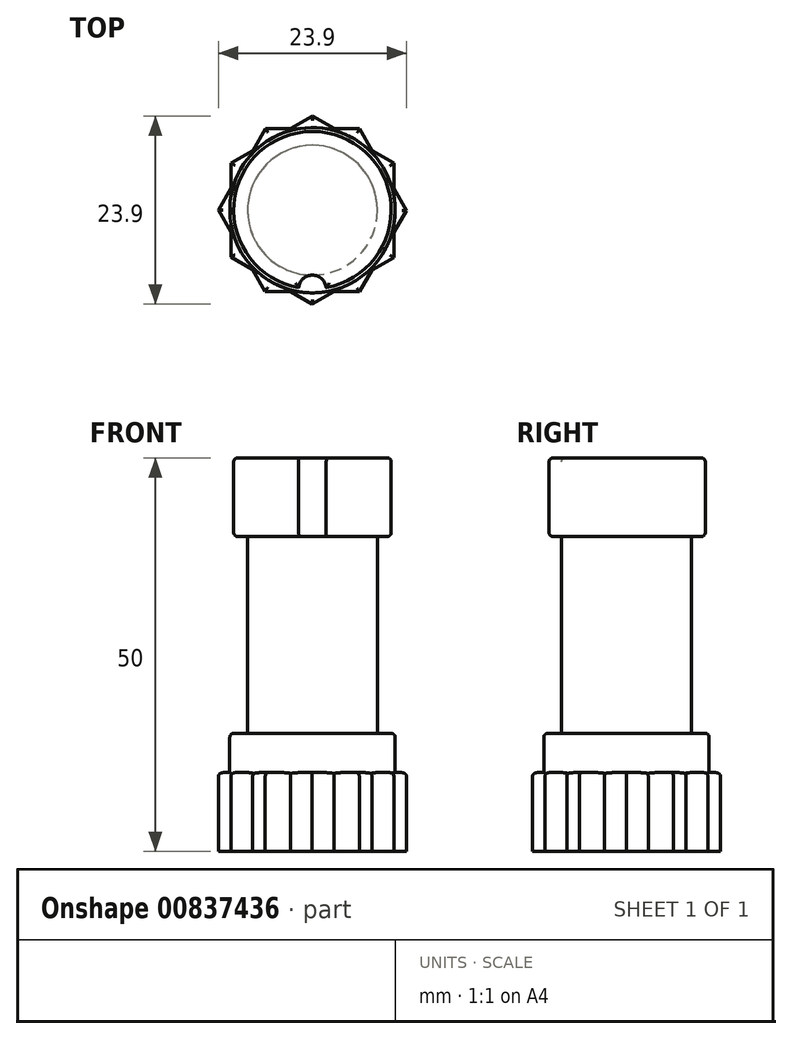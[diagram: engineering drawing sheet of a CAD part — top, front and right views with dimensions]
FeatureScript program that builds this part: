
annotation { "Feature Type Name" : "Feature", "Feature Type Description" : "" }
export const myFeature = defineFeature(function(context is Context, id is Id, definition is map)
    precondition{}
    {
        {
            var Q0;
            Q0=qCreatedBy(makeId("Top.planeOp"),FACE);
            var sketch = newSketch(context, id + "F0", { "sketchPlane" : qUnion([Q0])});
            skCircle(sketch, "E0.cCircle", {"center": v(0, 0) * mm, "radius": 11.95 * mm, "construction": true});
            skLineSegment(sketch, "E0.0", {"start": v(10.36, 5.96) * mm, "end": v(10.36, 2.75) * mm});
            skLineSegment(sketch, "E0.1", {"start": v(10.34, -6) * mm, "end": v(7.56, -7.6) * mm});
            skLineSegment(sketch, "E0.2", {"start": v(-0.02, -11.95) * mm, "end": v(-2.8, -10.34) * mm});
            skLineSegment(sketch, "E0.3", {"start": v(-10.36, -5.96) * mm, "end": v(-10.36, -2.75) * mm});
            skLineSegment(sketch, "E0.4", {"start": v(-10.34, 6) * mm, "end": v(-7.56, 7.6) * mm});
            skLineSegment(sketch, "E0.5", {"start": v(0.02, 11.95) * mm, "end": v(2.8, 10.34) * mm});
            skLineSegment(sketch, "E1", {"start": v(6, 10.34) * mm, "end": v(6.72, 11.59) * mm, "construction": true});
            skLineSegment(sketch, "E2.0", {"start": v(6, 10.34) * mm, "end": v(7.6, 7.56) * mm});
            skLineSegment(sketch, "E2.1", {"start": v(11.95, -0.02) * mm, "end": v(10.34, -2.8) * mm});
            skLineSegment(sketch, "E2.2", {"start": v(5.96, -10.36) * mm, "end": v(2.75, -10.36) * mm});
            skLineSegment(sketch, "E2.3", {"start": v(-6, -10.34) * mm, "end": v(-7.6, -7.56) * mm});
            skLineSegment(sketch, "E2.4", {"start": v(-11.95, 0.02) * mm, "end": v(-10.34, 2.8) * mm});
            skLineSegment(sketch, "E2.5", {"start": v(-5.96, 10.36) * mm, "end": v(-2.75, 10.36) * mm});
            skLineSegment(sketch, "E3.trimOffspring", {"start": v(-7.6, -7.56) * mm, "end": v(-10.36, -5.96) * mm});
            skPoint(sketch, "E4.orphan", {"position": v(-5.2, -8.95) * mm});
            skLineSegment(sketch, "E5.trimOffspring", {"start": v(-10.36, -2.75) * mm, "end": v(-11.95, 0.02) * mm});
            skLineSegment(sketch, "E6.trimOffspring", {"start": v(-2.8, -10.34) * mm, "end": v(-6, -10.34) * mm});
            skLineSegment(sketch, "E7.trimOffspring", {"start": v(2.75, -10.36) * mm, "end": v(-0.02, -11.95) * mm});
            skLineSegment(sketch, "E8.trimOffspring", {"start": v(7.56, -7.6) * mm, "end": v(5.96, -10.36) * mm});
            skLineSegment(sketch, "E9.trimOffspring", {"start": v(-10.34, 2.8) * mm, "end": v(-10.34, 6) * mm});
            skLineSegment(sketch, "E10.trimOffspring", {"start": v(-7.56, 7.6) * mm, "end": v(-5.96, 10.36) * mm});
            skLineSegment(sketch, "E11.trimOffspring", {"start": v(-2.75, 10.36) * mm, "end": v(0.02, 11.95) * mm});
            skLineSegment(sketch, "E12.trimOffspring", {"start": v(2.8, 10.34) * mm, "end": v(6, 10.34) * mm});
            skLineSegment(sketch, "E13.trimOffspring", {"start": v(7.6, 7.56) * mm, "end": v(10.36, 5.96) * mm});
            skPoint(sketch, "E14.orphan", {"position": v(5.2, 8.95) * mm});
            skLineSegment(sketch, "E15.trimOffspring", {"start": v(10.36, 2.75) * mm, "end": v(11.95, -0.02) * mm});
            skLineSegment(sketch, "E16.trimOffspring", {"start": v(10.34, -2.8) * mm, "end": v(10.34, -6) * mm});
            skSolve(sketch);
        }
        {
            var Q0;
            Q0=makeQuery(id+"F0.imprint","IMPRINT",FACE,{"disambiguationData":[TD([[makeQuery(id+"F0.imprint","IMPRINT",EDGE,{"derivedFrom":sQuery(id+"F0.wireOp",EDGE,"E0.0")}),-1.0]])]});
            extrude(context, id + "F1", {"entities" : qUnion([Q0]), "depth" : 10 * mm, "offsetDistance" : 25 * mm});
        }
        {
            var Q0;
            Q0=makeQuery(id+"F1.opExtrude","CAP_FACE",FACE,{"disambiguationData":[OSD([sQuery(id+"F0.wireOp",EDGE,"E0.0"),sQuery(id+"F0.wireOp",EDGE,"E0.1"),sQuery(id+"F0.wireOp",EDGE,"E0.2"),sQuery(id+"F0.wireOp",EDGE,"E0.3"),sQuery(id+"F0.wireOp",EDGE,"E0.4"),sQuery(id+"F0.wireOp",EDGE,"E0.5"),sQuery(id+"F0.wireOp",EDGE,"E2.0"),sQuery(id+"F0.wireOp",EDGE,"E2.1"),sQuery(id+"F0.wireOp",EDGE,"E2.2"),sQuery(id+"F0.wireOp",EDGE,"E2.3"),sQuery(id+"F0.wireOp",EDGE,"E2.4"),sQuery(id+"F0.wireOp",EDGE,"E2.5"),sQuery(id+"F0.wireOp",EDGE,"E3.trimOffspring"),sQuery(id+"F0.wireOp",EDGE,"E5.trimOffspring"),sQuery(id+"F0.wireOp",EDGE,"E6.trimOffspring"),sQuery(id+"F0.wireOp",EDGE,"E7.trimOffspring"),sQuery(id+"F0.wireOp",EDGE,"E8.trimOffspring"),sQuery(id+"F0.wireOp",EDGE,"E9.trimOffspring"),sQuery(id+"F0.wireOp",EDGE,"E10.trimOffspring"),sQuery(id+"F0.wireOp",EDGE,"E11.trimOffspring"),sQuery(id+"F0.wireOp",EDGE,"E12.trimOffspring"),sQuery(id+"F0.wireOp",EDGE,"E13.trimOffspring"),sQuery(id+"F0.wireOp",EDGE,"E15.trimOffspring"),sQuery(id+"F0.wireOp",EDGE,"E16.trimOffspring")])],"isStart":false});
            var sketch = newSketch(context, id + "F2", { "sketchPlane" : qUnion([Q0])});
            skLineSegment(sketch, "E17", {"start": v(-10.36, -2.75) * mm, "end": v(10.36, 2.75) * mm, "construction": true});
            skLineSegment(sketch, "E18", {"start": v(2.75, -10.36) * mm, "end": v(-2.75, 10.36) * mm, "construction": true});
            skCircle(sketch, "E19", {"center": v(0, 0) * mm, "radius": 10.5 * mm});
            skSolve(sketch);
        }
        {
            var Q0;
            Q0=makeQuery(id+"F2.imprint","IMPRINT",FACE,{"disambiguationData":[TD([[makeQuery(id+"F2.imprint","IMPRINT",EDGE,{"derivedFrom":sQuery(id+"F2.wireOp",EDGE,"E19")}),1.0]])]});
            extrude(context, id + "F3", {"entities" : qUnion([Q0]), "operationType" : NewBodyOperationType.ADD, "depth" : 5 * mm, "offsetDistance" : 25 * mm});
        }
        {
            var Q0;
            Q0=makeQuery(id+"F1.opExtrude","CAP_EDGE",EDGE,{"disambiguationData":[OSD([sQuery(id+"F0.wireOp",EDGE,"E2.5")])],"isStart":false});
            var Q1;
            Q1=makeQuery(id+"F1.opExtrude","CAP_EDGE",EDGE,{"disambiguationData":[OSD([sQuery(id+"F0.wireOp",EDGE,"E10.trimOffspring")])],"isStart":false});
            var Q2;
            Q2=makeQuery(id+"F1.opExtrude","CAP_EDGE",EDGE,{"disambiguationData":[OSD([sQuery(id+"F0.wireOp",EDGE,"E0.4")])],"isStart":false});
            var Q3;
            Q3=makeQuery(id+"F1.opExtrude","CAP_EDGE",EDGE,{"disambiguationData":[OSD([sQuery(id+"F0.wireOp",EDGE,"E9.trimOffspring")])],"isStart":false});
            var Q4;
            Q4=makeQuery(id+"F1.opExtrude","CAP_EDGE",EDGE,{"disambiguationData":[OSD([sQuery(id+"F0.wireOp",EDGE,"E2.4")])],"isStart":false});
            var Q5;
            Q5=makeQuery(id+"F1.opExtrude","CAP_EDGE",EDGE,{"disambiguationData":[OSD([sQuery(id+"F0.wireOp",EDGE,"E5.trimOffspring")])],"isStart":false});
            var Q6;
            Q6=makeQuery(id+"F1.opExtrude","CAP_EDGE",EDGE,{"disambiguationData":[OSD([sQuery(id+"F0.wireOp",EDGE,"E0.3")])],"isStart":false});
            var Q7;
            Q7=makeQuery(id+"F1.opExtrude","CAP_EDGE",EDGE,{"disambiguationData":[OSD([sQuery(id+"F0.wireOp",EDGE,"E3.trimOffspring")])],"isStart":false});
            var Q8;
            Q8=makeQuery(id+"F1.opExtrude","CAP_EDGE",EDGE,{"disambiguationData":[OSD([sQuery(id+"F0.wireOp",EDGE,"E2.3")])],"isStart":false});
            var Q9;
            Q9=makeQuery(id+"F1.opExtrude","CAP_EDGE",EDGE,{"disambiguationData":[OSD([sQuery(id+"F0.wireOp",EDGE,"E6.trimOffspring")])],"isStart":false});
            var Q10;
            Q10=makeQuery(id+"F1.opExtrude","CAP_EDGE",EDGE,{"disambiguationData":[OSD([sQuery(id+"F0.wireOp",EDGE,"E0.2")])],"isStart":false});
            var Q11;
            Q11=makeQuery(id+"F1.opExtrude","CAP_EDGE",EDGE,{"disambiguationData":[OSD([sQuery(id+"F0.wireOp",EDGE,"E7.trimOffspring")])],"isStart":false});
            var Q12;
            Q12=makeQuery(id+"F1.opExtrude","CAP_EDGE",EDGE,{"disambiguationData":[OSD([sQuery(id+"F0.wireOp",EDGE,"E2.2")])],"isStart":false});
            var Q13;
            Q13=makeQuery(id+"F1.opExtrude","CAP_EDGE",EDGE,{"disambiguationData":[OSD([sQuery(id+"F0.wireOp",EDGE,"E8.trimOffspring")])],"isStart":false});
            var Q14;
            Q14=makeQuery(id+"F1.opExtrude","CAP_EDGE",EDGE,{"disambiguationData":[OSD([sQuery(id+"F0.wireOp",EDGE,"E0.1")])],"isStart":false});
            var Q15;
            Q15=makeQuery(id+"F1.opExtrude","CAP_EDGE",EDGE,{"disambiguationData":[OSD([sQuery(id+"F0.wireOp",EDGE,"E16.trimOffspring")])],"isStart":false});
            var Q16;
            Q16=makeQuery(id+"F1.opExtrude","CAP_EDGE",EDGE,{"disambiguationData":[OSD([sQuery(id+"F0.wireOp",EDGE,"E2.1")])],"isStart":false});
            var Q17;
            Q17=makeQuery(id+"F1.opExtrude","CAP_EDGE",EDGE,{"disambiguationData":[OSD([sQuery(id+"F0.wireOp",EDGE,"E15.trimOffspring")])],"isStart":false});
            var Q18;
            Q18=makeQuery(id+"F1.opExtrude","CAP_EDGE",EDGE,{"disambiguationData":[OSD([sQuery(id+"F0.wireOp",EDGE,"E0.0")])],"isStart":false});
            var Q19;
            Q19=makeQuery(id+"F1.opExtrude","CAP_EDGE",EDGE,{"disambiguationData":[OSD([sQuery(id+"F0.wireOp",EDGE,"E13.trimOffspring")])],"isStart":false});
            var Q20;
            Q20=makeQuery(id+"F1.opExtrude","CAP_EDGE",EDGE,{"disambiguationData":[OSD([sQuery(id+"F0.wireOp",EDGE,"E2.0")])],"isStart":false});
            var Q21;
            Q21=makeQuery(id+"F1.opExtrude","CAP_EDGE",EDGE,{"disambiguationData":[OSD([sQuery(id+"F0.wireOp",EDGE,"E12.trimOffspring")])],"isStart":false});
            var Q22;
            Q22=makeQuery(id+"F1.opExtrude","CAP_EDGE",EDGE,{"disambiguationData":[OSD([sQuery(id+"F0.wireOp",EDGE,"E0.5")])],"isStart":false});
            var Q23;
            Q23=makeQuery(id+"F1.opExtrude","CAP_EDGE",EDGE,{"disambiguationData":[OSD([sQuery(id+"F0.wireOp",EDGE,"E11.trimOffspring")])],"isStart":false});
            fillet(context, id + "F4", {"entities" : qUnion([Q0, Q1, Q2, Q3, Q4, Q5, Q6, Q7, Q8, Q9, Q10, Q11, Q12, Q13, Q14, Q15, Q16, Q17, Q18, Q19, Q20, Q21, Q22, Q23]), "radius" : .5 * mm, "tangentPropagation" : true, "allowEdgeOverflow" : false});
        }
        {
            var Q0;
            Q0=makeQuery(id+"F3.opExtrude","CAP_FACE",FACE,{"disambiguationData":[OSD([sQuery(id+"F2.wireOp",EDGE,"E19")])],"isStart":false});
            var sketch = newSketch(context, id + "F5", { "sketchPlane" : qUnion([Q0])});
            skCircle(sketch, "E20", {"center": v(0, 0) * mm, "radius": 8.25 * mm});
            skSolve(sketch);
        }
        {
            var Q0;
            Q0=makeQuery(id+"F5.imprint","IMPRINT",FACE,{"disambiguationData":[TD([[makeQuery(id+"F5.imprint","IMPRINT",EDGE,{"derivedFrom":sQuery(id+"F5.wireOp",EDGE,"E20")}),1.0]])]});
            extrude(context, id + "F6", {"entities" : qUnion([Q0]), "operationType" : NewBodyOperationType.ADD, "depth" : 25 * mm, "offsetDistance" : 25 * mm});
        }
        {
            var Q0;
            Q0=makeQuery(id+"F6.opExtrude","CAP_FACE",FACE,{"disambiguationData":[OSD([sQuery(id+"F5.wireOp",EDGE,"E20")])],"isStart":false});
            var sketch = newSketch(context, id + "F7", { "sketchPlane" : qUnion([Q0])});
            skCircle(sketch, "E21", {"center": v(0, 0) * mm, "radius": 10 * mm});
            skSolve(sketch);
        }
        {
            var Q0;
            Q0=makeQuery(id+"F7.imprint","IMPRINT",FACE,{"disambiguationData":[TD([[makeQuery(id+"F7.imprint","IMPRINT",EDGE,{"derivedFrom":sQuery(id+"F7.wireOp",EDGE,"E21")}),1.0]])]});
            var Q1;
            Q1=makeQuery(id+"F7.imprint","IMPRINT",FACE,{"disambiguationData":[TD([[makeQuery(id+"F7.imprint","IMPRINT",EDGE,{"derivedFrom":makeQuery(id+"F6.opExtrude","CAP_EDGE",EDGE,{"disambiguationData":[OSD([sQuery(id+"F5.wireOp",EDGE,"E20")])],"isStart":false})}),1.0]])]});
            extrude(context, id + "F8", {"entities" : qUnion([Q0, Q1]), "operationType" : NewBodyOperationType.ADD, "depth" : 10 * mm, "offsetDistance" : 25 * mm});
        }
        {
            var Q0;
            Q0=makeQuery(id+"F8.opExtrude","CAP_FACE",FACE,{"disambiguationData":[OSD([sQuery(id+"F7.wireOp",EDGE,"E21")])],"isStart":true});
            var sketch = newSketch(context, id + "F9", { "sketchPlane" : qUnion([Q0])});
            skLineSegment(sketch, "E22", {"start": v(0, 10) * mm, "end": v(0, 8.25) * mm, "construction": true});
            skArc(sketch, "E23", {"start": v(0, 8.25) * mm, "mid": v(1.18, 8.7) * mm, "end": v(1.74, 9.85) * mm});
            skArc(sketch, "E24", {"start": v(0, 8.25) * mm, "mid": v(-1.18, 8.7) * mm, "end": v(-1.74, 9.85) * mm});
            skSolve(sketch);
        }
        {
            var Q0;
            {var subQ0=sQuery(id+"F9.wireOp",EDGE,"E23");Q0=makeQuery(id+"F9.imprint","IMPRINT",FACE,{"disambiguationData":[TD([[makeQuery(id+"F9.imprint","IMPRINT",EDGE,{"derivedFrom":subQ0}),1.0]])]});}
            extrude(context, id + "F10", {"entities" : qUnion([Q0]), "operationType" : NewBodyOperationType.REMOVE, "oppositeDirection" : true, "depth" : 25 * mm, "offsetDistance" : 25 * mm});
        }
        {
            var Q0;
            Q0=makeQuery(id+"F8.opExtrude","CAP_EDGE",EDGE,{"disambiguationData":[OSD([sQuery(id+"F7.wireOp",EDGE,"E21")])],"isStart":false});
            var Q1;
            Q1=makeQuery(id+"F10.boolean.opBoolean","INTERSECT",EDGE,{"derivedFrom":[makeQuery(id+"F8.opExtrude","CAP_FACE",FACE,{"disambiguationData":[OSD([sQuery(id+"F7.wireOp",EDGE,"E21")])],"isStart":false}),makeQuery(id+"F10.opExtrude","SWEPT_FACE",FACE,{"disambiguationData":[OSD([sQuery(id+"F9.wireOp",EDGE,"E23"),sQuery(id+"F9.wireOp",EDGE,"E24")])]})]});
            var Q2;
            Q2=makeQuery(id+"F10.boolean.opBoolean","COPY",EDGE,{"derivedFrom":makeQuery(id+"F10.opExtrude","SWEPT_EDGE",EDGE,{"disambiguationData":[OSD([sQuery(id+"F7.wireOp",EDGE,"E21"),sQuery(id+"F9.wireOp",EDGE,"E24")])]})});
            var Q3;
            Q3=makeQuery(id+"F10.boolean.opBoolean","COPY",EDGE,{"derivedFrom":makeQuery(id+"F10.opExtrude","SWEPT_EDGE",EDGE,{"disambiguationData":[OSD([sQuery(id+"F7.wireOp",EDGE,"E21"),sQuery(id+"F9.wireOp",EDGE,"E23")])]})});
            var Q4;
            Q4=makeQuery(id+"F8.opExtrude","CAP_EDGE",EDGE,{"disambiguationData":[OSD([sQuery(id+"F7.wireOp",EDGE,"E21")])],"isStart":true});
            var Q5;
            Q5=makeQuery(id+"F10.boolean.opBoolean","COPY",EDGE,{"disambiguationData":[OD(1.0)],"derivedFrom":makeQuery(id+"F10.opExtrude","CAP_EDGE",EDGE,{"disambiguationData":[OSD([sQuery(id+"F9.wireOp",EDGE,"E23"),sQuery(id+"F9.wireOp",EDGE,"E24")])],"isStart":true})});
            var Q6;
            Q6=makeQuery(id+"F10.boolean.opBoolean","COPY",EDGE,{"disambiguationData":[OD(0.0)],"derivedFrom":makeQuery(id+"F10.opExtrude","CAP_EDGE",EDGE,{"disambiguationData":[OSD([sQuery(id+"F9.wireOp",EDGE,"E23"),sQuery(id+"F9.wireOp",EDGE,"E24")])],"isStart":true})});
            fillet(context, id + "F11", {"entities" : qUnion([Q0, Q1, Q2, Q3, Q4, Q5, Q6]), "radius" : .5 * mm, "tangentPropagation" : true, "allowEdgeOverflow" : false});
        }
        {
            var Q0;
            Q0=makeQuery(id+"F6.opExtrude","CAP_EDGE",EDGE,{"disambiguationData":[OSD([sQuery(id+"F5.wireOp",EDGE,"E20")])],"isStart":true});
            var Q1;
            Q1=makeQuery(id+"F3.opExtrude","CAP_EDGE",EDGE,{"disambiguationData":[OSD([sQuery(id+"F2.wireOp",EDGE,"E19")])],"isStart":false});
            fillet(context, id + "F12", {"entities" : qUnion([Q0, Q1]), "radius" : .5 * mm, "tangentPropagation" : true, "allowEdgeOverflow" : false});
        }
    });
